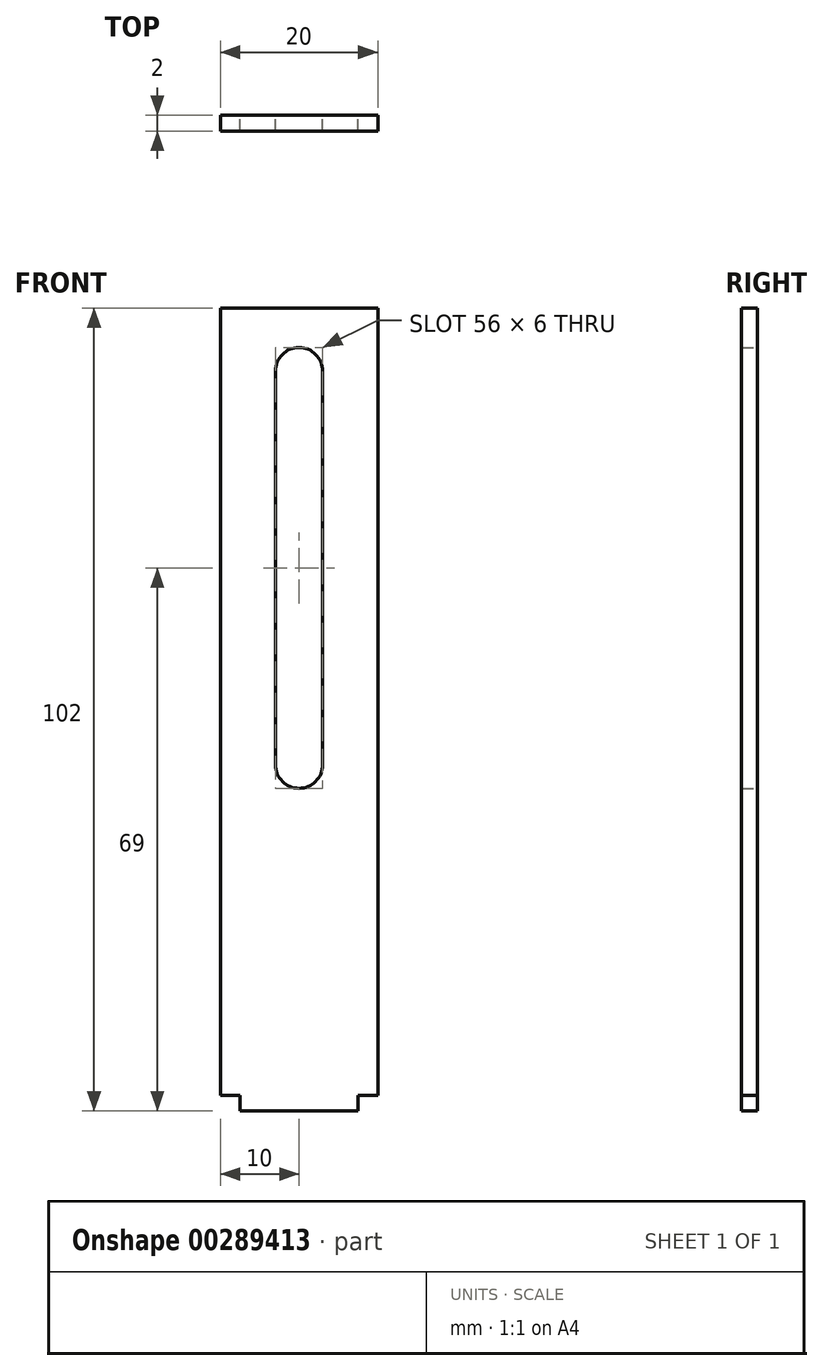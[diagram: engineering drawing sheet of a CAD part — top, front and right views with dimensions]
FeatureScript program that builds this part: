
annotation { "Feature Type Name" : "Feature", "Feature Type Description" : "" }
export const myFeature = defineFeature(function(context is Context, id is Id, definition is map)
    precondition{}
    {
        {
            var Q0;
            Q0=qCreatedBy(makeId("Front.planeOp"),FACE);
            var sketch = newSketch(context, id + "F0", { "sketchPlane" : qUnion([Q0])});
            skLineSegment(sketch, "E0", {"start": v(0, 0) * mm, "end": v(15, 0) * mm});
            skLineSegment(sketch, "E1", {"start": v(15, 0) * mm, "end": v(15, 2) * mm});
            skLineSegment(sketch, "E2", {"start": v(15, 2) * mm, "end": v(17.5, 2) * mm});
            skLineSegment(sketch, "E3", {"start": v(17.5, 2) * mm, "end": v(17.5, 102) * mm});
            skLineSegment(sketch, "E4", {"start": v(17.5, 102) * mm, "end": v(-2.5, 102) * mm});
            skLineSegment(sketch, "E5", {"start": v(-2.5, 102) * mm, "end": v(-2.5, 2) * mm});
            skLineSegment(sketch, "E6", {"start": v(-2.5, 2) * mm, "end": v(0, 2) * mm});
            skLineSegment(sketch, "E7", {"start": v(0, 2) * mm, "end": v(0, 0) * mm});
            skLineSegment(sketch, "E8.bottom", {"start": v(4.5, 94) * mm, "end": v(10.5, 94) * mm});
            skLineSegment(sketch, "E8.top", {"start": v(4.5, 44) * mm, "end": v(10.5, 44) * mm});
            skLineSegment(sketch, "E8.left", {"start": v(4.5, 94) * mm, "end": v(4.5, 44) * mm});
            skLineSegment(sketch, "E8.right", {"start": v(10.5, 94) * mm, "end": v(10.5, 44) * mm});
            skArc(sketch, "E9", {"start": v(4.5, 44) * mm, "mid": v(7.5, 41) * mm, "end": v(10.5, 44) * mm});
            skArc(sketch, "E10", {"start": v(10.5, 94) * mm, "mid": v(7.5, 97) * mm, "end": v(4.5, 94) * mm});
            skSolve(sketch);
        }
        {
            var Q0;
            Q0 = qSketchRegion(id + "F0", true);
            extrude(context, id + "F1", {"entities" : qUnion([Q0]), "depth" : 2 * mm});
        }
    });
